# Revit family: Geberit Bambini područje za igru i pranje, za dve armature za umivaonik_PRO_581292
name_source: partatom
category: Plumbing Fixtures
revit_build: Autodesk Revit 2018 (Build: 20190510_1515(x64)
units: mm (PartAtom-declared; Revit-internal decimal feet)

## family parameters
Always vertical = Yes
Cut with Voids When Loaded = No
OmniClass Number = 23.45.05.21
OmniClass Title = Plumbing Fixtures - Sanitary Disposal Units
Part Type = Normal
Room Calculation Point = Yes
Round Connector Dimension = Use Diameter
Shared = No
Work Plane-Based = No

## types (2) — shared parameters
BIM datoteka, datum izmene = 2020.05.18
BIM datoteka, proizvođač = Geberit
BIM datoteka, verzija = GEB MG 1.2
Boja / površina = alpsko bela
CW Connection = Yes
Description = Geberit Bambini područje za igru i pranje, za dve armature za umivaonik
GEB_culture = sr-RS
GEB_generic_description = Bathroom collection
GEB_generic_manufacturer = generic
GEB_pimversion = 22.02.12
GEB_processing_type = T
GEB_reference = PRO_581292
GEB_translations = {"ATT_10673":"EAN code basic data","ATT_10882":"Materijal proizvoda","ATT_459792":"Boja / površina","applicationPurposes":"Namene","application_range":"Oblast primene","brandName":"Robna marka","characteristics":"Svojstva","content_creator":"BIM datoteka, proizvođač","content_date_changed":"BIM datoteka, datum izmene","content_version":"BIM datoteka, verzija","key 1000":"Broj artikla","name":"Naziv","productBrand":"Robna marka proizvoda","scopeOfDelivery":"Obim isporuke","type":"Tip","fixed_material":"Osnovni materijal"}
HW Connection = No
IfcDescription = Geberit Bambini područje za igru i pranje, za dve armature za umivaonik
IfcExportAs = IfcSanitaryTerminal
IfcExportType = WASHHANDBASIN
LOD300 = No
LOD400 = Yes
Manufacturer = Geberit
Materijal proizvoda = Varicor®
Namene = Za montažu na montažne ploče
Za decu
Za škole, ustanove za zbrinjavanje dece i druge obrazovne ustanove
Naziv = Geberit Bambini područje za igru i pranje, za dve armature za umivaonik
Oblast primene = Plumbing fixture
Osnovni materijal = Geberit, Plastic, Opaque white
Robna marka = Geberit
Svojstva = 2 mesta za pranje
Smanjena dubina
Talasasta ivica za jednostavan pristup armaturi
Oble ivice za sprečavanje povreda
Antibakterijski
Otporan na udarce
Otporno na grebanje
Jednostavno čišćenje
Površinska opravka bez varova
Vent Connection = No
Waste Connection = Yes
outlet_flow = 0.0 L/s

## per-type parameters (varying)
| type | 430200016_0_view | 501669_0_view | Broj artikla | EAN code basic data |
| 501.669.11.1 Geberit Bambini područje za igru i pranje, za dve armature za umivaonik | No | Yes | 501.669.11.1 | 4025410945631 |
| 430200016 Geberit Bambini područje za igru i pranje, za dve armature za umivaonik | Yes | No | 430200016 | 4022009330397 |

## geometry (parser evidence)
native form markers: Blend x8, Sweep x18
no freeform markers — native parametric forms only
